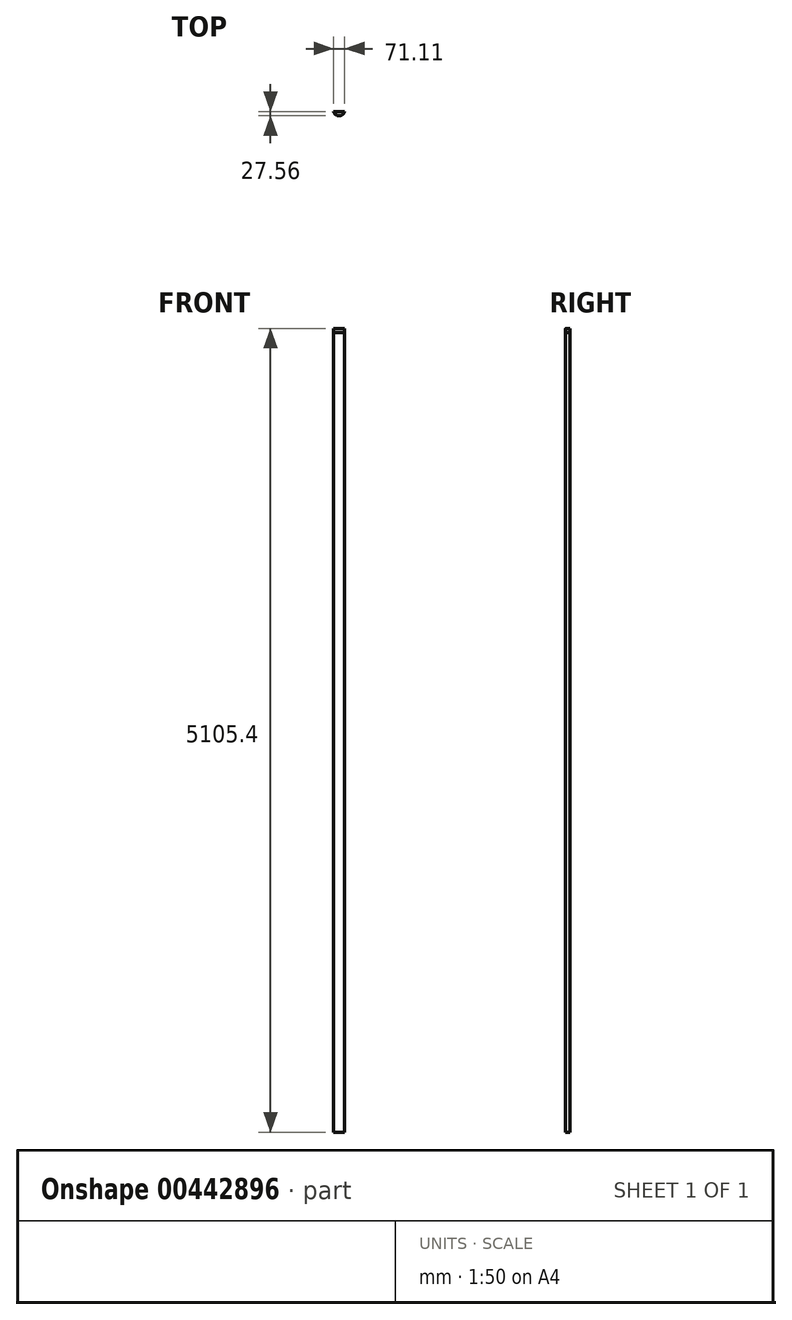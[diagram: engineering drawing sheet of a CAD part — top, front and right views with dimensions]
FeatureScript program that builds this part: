
annotation { "Feature Type Name" : "Feature", "Feature Type Description" : "" }
export const myFeature = defineFeature(function(context is Context, id is Id, definition is map)
    precondition{}
    {
        {
            var Q0;
            Q0=qCreatedBy(makeId("Top.planeOp"),FACE);
            var sketch = newSketch(context, id + "F0", { "sketchPlane" : qUnion([Q0])});
            skLineSegment(sketch, "E0", {"start": v(0, 0) * mm, "end": v(0, -62.72) * mm});
            skLineSegment(sketch, "E1", {"start": v(0, -62.72) * mm, "end": v(0, 63.22) * mm});
            skLineSegment(sketch, "E2", {"start": v(0, 63.22) * mm, "end": v(0, 0) * mm});
            skLineSegment(sketch, "E3", {"start": v(0, 0) * mm, "end": v(54.68, 0) * mm});
            skLineSegment(sketch, "E4", {"start": v(54.68, 0) * mm, "end": v(-50.9, 0) * mm});
            skPoint(sketch, "E4.endSnap0", {"position": v(27.34, 0) * mm});
            skLineSegment(sketch, "E5", {"start": v(-50.9, 0) * mm, "end": v(0, 0) * mm});
            skArc(sketch, "E6", {"start": v(-37.83, 22.04) * mm, "mid": v(-2.99, -27.55) * mm, "end": v(30.58, 22.92) * mm});
            skSolve(sketch);
        }
        {
            var Q0;
            Q0=qCreatedBy(makeId("Front.planeOp"),FACE);
            var sketch = newSketch(context, id + "F1", { "sketchPlane" : qUnion([Q0])});
            skLineSegment(sketch, "E7", {"start": v(0, 0) * mm, "end": v(0, 48.76) * mm});
            skLineSegment(sketch, "E8", {"start": v(0, 48.76) * mm, "end": v(0, -41.56) * mm});
            skSolve(sketch);
        }
        {
            var Q0;
            {var subQ0=sQuery(id+"F0.wireOp",EDGE,"E4");var subQ3=sQuery(id+"F0.wireOp",EDGE,"E6");var subQ5=makeQuery(id+"F0.imprint","INTERSECT",VERTEX,{"derivedFrom":[subQ0,subQ3]});Q0=makeQuery(id+"F0.imprint","IMPRINT",FACE,{"disambiguationData":[TD([[makeQuery(id+"F0.imprint","IMPRINT",EDGE,{"disambiguationData":[TD([[subQ5,1.0]])],"derivedFrom":subQ3}),1.0]])]});}
            var Q1;
            {var subQ0=sQuery(id+"F0.wireOp",EDGE,"E5");var subQ3=sQuery(id+"F0.wireOp",EDGE,"E6");var subQ5=makeQuery(id+"F0.imprint","INTERSECT",VERTEX,{"derivedFrom":[subQ0,subQ3]});Q1=makeQuery(id+"F0.imprint","IMPRINT",FACE,{"disambiguationData":[TD([[makeQuery(id+"F0.imprint","IMPRINT",EDGE,{"disambiguationData":[TD([[subQ5,-1.0]])],"derivedFrom":subQ3}),1.0]])]});}
            extrude(context, id + "F2", {"entities" : qUnion([Q0, Q1]), "depth" : 25.4 * mm});
        }
        {
            var Q0;
            Q0 = qSketchRegion(id + "F1", true);
            var Q1;
            Q1=makeQuery(id+"F2.opExtrude","CAP_FACE",FACE,{"disambiguationData":[OSD([sQuery(id+"F0.wireOp",EDGE,"E4"),sQuery(id+"F0.wireOp",EDGE,"E5"),sQuery(id+"F0.wireOp",EDGE,"E6")])],"isStart":true});
            extrude(context, id + "F3", {"entities" : qUnion([Q0, Q1]), "depth" : 5080 * mm});
        }
    });
